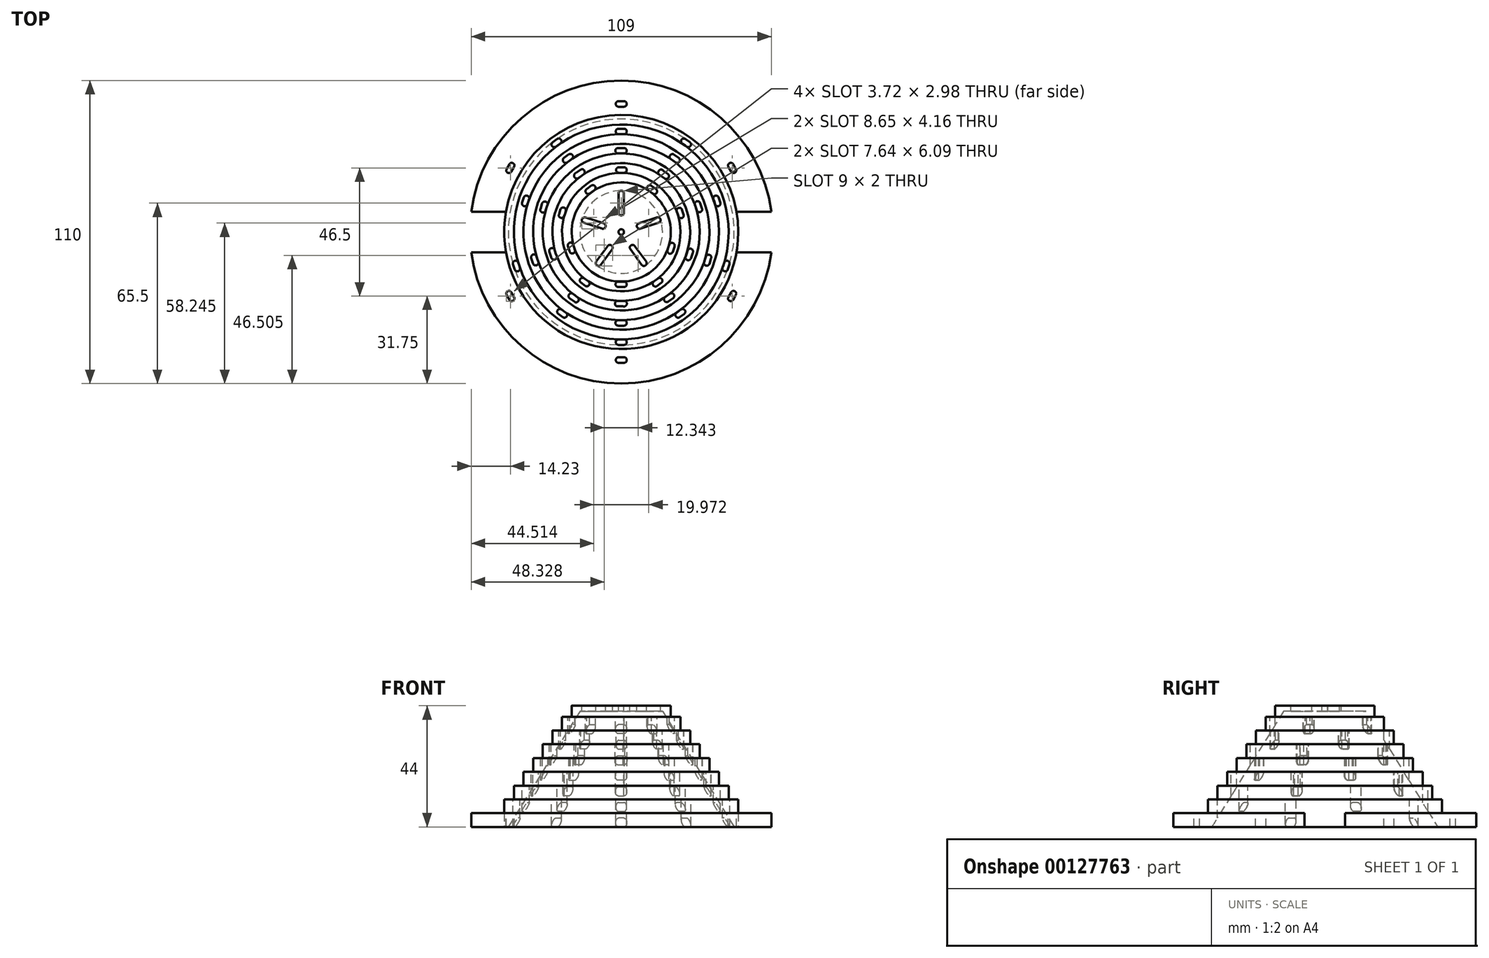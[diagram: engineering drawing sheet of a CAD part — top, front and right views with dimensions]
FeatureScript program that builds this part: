
annotation { "Feature Type Name" : "Feature", "Feature Type Description" : "" }
export const myFeature = defineFeature(function(context is Context, id is Id, definition is map)
    precondition{}
    {
        {
            var Q0;
            Q0=qCreatedBy(makeId("Top.planeOp"),FACE);
            var sketch = newSketch(context, id + "F0", { "sketchPlane" : qUnion([Q0])});
            skCircle(sketch, "E0", {"center": v(0, 0) * mm, "radius": 55 * mm});
            skSolve(sketch);
        }
        {
            var Q0;
            Q0 = qSketchRegion(id + "F0", true);
            extrude(context, id + "F1", {"entities" : qUnion([Q0]), "depth" : 5 * mm});
        }
        {
            var Q0;
            Q0=makeQuery(id+"F1.opExtrude","CAP_FACE",FACE,{"disambiguationData":[OSD([sQuery(id+"F0.wireOp",EDGE,"E0")])],"isStart":false});
            var sketch = newSketch(context, id + "F2", { "sketchPlane" : qUnion([Q0])});
            skCircle(sketch, "E1.0", {"center": v(0, 0) * mm, "radius": 42.5 * mm});
            skSolve(sketch);
        }
        {
            var Q0;
            Q0 = qSketchRegion(id + "F2", true);
            extrude(context, id + "F3", {"entities" : qUnion([Q0]), "operationType" : NewBodyOperationType.ADD, "depth" : 5 * mm});
        }
        {
            var Q0;
            Q0=makeQuery(id+"F3.opExtrude","CAP_FACE",FACE,{"disambiguationData":[OSD([sQuery(id+"F2.wireOp",EDGE,"E1.0")])],"isStart":false});
            var sketch = newSketch(context, id + "F4", { "sketchPlane" : qUnion([Q0])});
            skLineSegment(sketch, "E2", {"start": v(0, 0) * mm, "end": v(0, -39) * mm, "construction": true});
            skLineSegment(sketch, "E3", {"start": v(-1, -39) * mm, "end": v(1, -39) * mm});
            skLineSegment(sketch, "E4", {"start": v(-1, -39) * mm, "end": v(-1, -40) * mm, "construction": true});
            skArc(sketch, "E5", {"start": v(-1, -39) * mm, "mid": v(-2, -40) * mm, "end": v(-1, -41) * mm});
            skArc(sketch, "E6.MirrorC", {"start": v(1, -39) * mm, "mid": v(2, -40) * mm, "end": v(1, -41) * mm});
            skLineSegment(sketch, "E7", {"start": v(-1, -41) * mm, "end": v(1, -41) * mm});
            skLineSegment(sketch, "E8.1.0", {"start": v(36.78, -13) * mm, "end": v(37.4, -11.1) * mm});
            skArc(sketch, "E8.1.1", {"start": v(36.78, -13) * mm, "mid": v(37.42, -14.26) * mm, "end": v(38.68, -13.62) * mm});
            skLineSegment(sketch, "E8.1.2", {"start": v(38.68, -13.62) * mm, "end": v(39.3, -11.72) * mm});
            skArc(sketch, "E8.1.3", {"start": v(37.4, -11.1) * mm, "mid": v(38.66, -10.46) * mm, "end": v(39.3, -11.72) * mm});
            skLineSegment(sketch, "E8.2.0", {"start": v(23.73, 30.96) * mm, "end": v(22.11, 32.14) * mm});
            skArc(sketch, "E8.2.1", {"start": v(23.73, 30.96) * mm, "mid": v(25.13, 31.19) * mm, "end": v(24.9, 32.58) * mm});
            skLineSegment(sketch, "E8.2.2", {"start": v(24.9, 32.58) * mm, "end": v(23.3, 33.76) * mm});
            skArc(sketch, "E8.2.3", {"start": v(22.11, 32.14) * mm, "mid": v(21.9, 33.54) * mm, "end": v(23.3, 33.76) * mm});
            skLineSegment(sketch, "E8.3.0", {"start": v(-22.11, 32.14) * mm, "end": v(-23.73, 30.96) * mm});
            skArc(sketch, "E8.3.1", {"start": v(-22.11, 32.14) * mm, "mid": v(-21.9, 33.54) * mm, "end": v(-23.3, 33.76) * mm});
            skLineSegment(sketch, "E8.3.2", {"start": v(-23.3, 33.76) * mm, "end": v(-24.9, 32.58) * mm});
            skArc(sketch, "E8.3.3", {"start": v(-23.73, 30.96) * mm, "mid": v(-25.13, 31.19) * mm, "end": v(-24.9, 32.58) * mm});
            skLineSegment(sketch, "E8.4.0", {"start": v(-37.4, -11.1) * mm, "end": v(-36.78, -13) * mm});
            skArc(sketch, "E8.4.1", {"start": v(-37.4, -11.1) * mm, "mid": v(-38.66, -10.46) * mm, "end": v(-39.3, -11.72) * mm});
            skLineSegment(sketch, "E8.4.2", {"start": v(-39.3, -11.72) * mm, "end": v(-38.68, -13.62) * mm});
            skArc(sketch, "E8.4.3", {"start": v(-36.78, -13) * mm, "mid": v(-37.42, -14.26) * mm, "end": v(-38.68, -13.62) * mm});
            skPoint(sketch, "E8.center", {"position": v(0, 0) * mm});
            skSolve(sketch);
        }
        {
            var Q0;
            Q0 = qSketchRegion(id + "F4", true);
            extrude(context, id + "F5", {"entities" : qUnion([Q0]), "operationType" : NewBodyOperationType.REMOVE, "endBound" : BoundingType.THROUGH_ALL, "oppositeDirection" : true, "depth" : 25 * mm});
        }
        {
            var Q0;
            Q0=makeQuery(id+"F1.opExtrude","CAP_FACE",FACE,{"disambiguationData":[OSD([sQuery(id+"F0.wireOp",EDGE,"E0")])],"isStart":false});
            var sketch = newSketch(context, id + "F6", { "sketchPlane" : qUnion([Q0])});
            skLineSegment(sketch, "E9", {"start": v(0, 0) * mm, "end": v(0, 45.5) * mm, "construction": true});
            skLineSegment(sketch, "E10", {"start": v(-1, 45.5) * mm, "end": v(1, 45.5) * mm});
            skLineSegment(sketch, "E11", {"start": v(-1, 45.5) * mm, "end": v(-1, 46.5) * mm, "construction": true});
            skArc(sketch, "E12", {"start": v(-1, 47.5) * mm, "mid": v(-2, 46.5) * mm, "end": v(-1, 45.5) * mm});
            skArc(sketch, "E13.MirrorC", {"start": v(1, 47.5) * mm, "mid": v(2, 46.5) * mm, "end": v(1, 45.5) * mm});
            skLineSegment(sketch, "E14", {"start": v(-1, 47.5) * mm, "end": v(1, 47.5) * mm});
            skArc(sketch, "E15.1.0", {"start": v(-41.64, 22.88) * mm, "mid": v(-41.27, 21.52) * mm, "end": v(-39.9, 21.88) * mm});
            skLineSegment(sketch, "E15.1.1", {"start": v(-41.64, 22.88) * mm, "end": v(-40.64, 24.62) * mm});
            skArc(sketch, "E15.1.2", {"start": v(-40.64, 24.62) * mm, "mid": v(-39.27, 24.98) * mm, "end": v(-38.9, 23.62) * mm});
            skLineSegment(sketch, "E15.1.3", {"start": v(-39.9, 21.88) * mm, "end": v(-38.9, 23.62) * mm});
            skArc(sketch, "E15.2.0", {"start": v(-40.64, -24.62) * mm, "mid": v(-39.27, -24.98) * mm, "end": v(-38.9, -23.62) * mm});
            skLineSegment(sketch, "E15.2.1", {"start": v(-40.64, -24.62) * mm, "end": v(-41.64, -22.88) * mm});
            skArc(sketch, "E15.2.2", {"start": v(-41.64, -22.88) * mm, "mid": v(-41.27, -21.52) * mm, "end": v(-39.9, -21.88) * mm});
            skLineSegment(sketch, "E15.2.3", {"start": v(-38.9, -23.62) * mm, "end": v(-39.9, -21.88) * mm});
            skArc(sketch, "E15.3.0", {"start": v(1, -47.5) * mm, "mid": v(2, -46.5) * mm, "end": v(1, -45.5) * mm});
            skLineSegment(sketch, "E15.3.1", {"start": v(1, -47.5) * mm, "end": v(-1, -47.5) * mm});
            skArc(sketch, "E15.3.2", {"start": v(-1, -47.5) * mm, "mid": v(-2, -46.5) * mm, "end": v(-1, -45.5) * mm});
            skLineSegment(sketch, "E15.3.3", {"start": v(1, -45.5) * mm, "end": v(-1, -45.5) * mm});
            skArc(sketch, "E15.4.0", {"start": v(41.64, -22.88) * mm, "mid": v(41.27, -21.52) * mm, "end": v(39.9, -21.88) * mm});
            skLineSegment(sketch, "E15.4.1", {"start": v(41.64, -22.88) * mm, "end": v(40.64, -24.62) * mm});
            skArc(sketch, "E15.4.2", {"start": v(40.64, -24.62) * mm, "mid": v(39.27, -24.98) * mm, "end": v(38.9, -23.62) * mm});
            skLineSegment(sketch, "E15.4.3", {"start": v(39.9, -21.88) * mm, "end": v(38.9, -23.62) * mm});
            skArc(sketch, "E15.5.0", {"start": v(40.64, 24.62) * mm, "mid": v(39.27, 24.98) * mm, "end": v(38.9, 23.62) * mm});
            skLineSegment(sketch, "E15.5.1", {"start": v(40.64, 24.62) * mm, "end": v(41.64, 22.88) * mm});
            skArc(sketch, "E15.5.2", {"start": v(41.64, 22.88) * mm, "mid": v(41.27, 21.52) * mm, "end": v(39.9, 21.88) * mm});
            skLineSegment(sketch, "E15.5.3", {"start": v(38.9, 23.62) * mm, "end": v(39.9, 21.88) * mm});
            skPoint(sketch, "E15.center", {"position": v(0, 0) * mm});
            skSolve(sketch);
        }
        {
            var Q0;
            Q0 = qSketchRegion(id + "F6", true);
            extrude(context, id + "F7", {"entities" : qUnion([Q0]), "operationType" : NewBodyOperationType.REMOVE, "endBound" : BoundingType.THROUGH_ALL, "oppositeDirection" : true, "depth" : 25 * mm});
        }
        {
            var Q0;
            Q0=makeQuery(id+"F3.opExtrude","CAP_FACE",FACE,{"disambiguationData":[OSD([sQuery(id+"F2.wireOp",EDGE,"E1.0")])],"isStart":false});
            var sketch = newSketch(context, id + "F8", { "sketchPlane" : qUnion([Q0])});
            skCircle(sketch, "E16.0", {"center": v(0, 0) * mm, "radius": 39 * mm});
            skSolve(sketch);
        }
        {
            var Q0;
            Q0 = qSketchRegion(id + "F8", true);
            extrude(context, id + "F9", {"entities" : qUnion([Q0]), "operationType" : NewBodyOperationType.ADD, "depth" : 5 * mm});
        }
        {
            var Q0;
            Q0=makeQuery(id+"F9.opExtrude","CAP_FACE",FACE,{"disambiguationData":[OSD([sQuery(id+"F8.wireOp",EDGE,"E16.0")])],"isStart":false});
            var sketch = newSketch(context, id + "F10", { "sketchPlane" : qUnion([Q0])});
            skLineSegment(sketch, "E17", {"start": v(0, 0) * mm, "end": v(0, 35.5) * mm, "construction": true});
            skLineSegment(sketch, "E18.0", {"start": v(1, 37.5) * mm, "end": v(-1, 37.5) * mm});
            skArc(sketch, "E19.0", {"start": v(-1, 37.5) * mm, "mid": v(-2, 36.5) * mm, "end": v(-1, 35.5) * mm});
            skLineSegment(sketch, "E20.0", {"start": v(1, 35.5) * mm, "end": v(-1, 35.5) * mm});
            skArc(sketch, "E21.0", {"start": v(1, 37.5) * mm, "mid": v(2, 36.5) * mm, "end": v(1, 35.5) * mm});
            skLineSegment(sketch, "E22.1.0", {"start": v(-35.36, 12.54) * mm, "end": v(-35.97, 10.64) * mm});
            skArc(sketch, "E22.1.1", {"start": v(-35.97, 10.64) * mm, "mid": v(-35.33, 9.38) * mm, "end": v(-34.07, 10.02) * mm});
            skLineSegment(sketch, "E22.1.2", {"start": v(-33.45, 11.92) * mm, "end": v(-34.07, 10.02) * mm});
            skArc(sketch, "E22.1.3", {"start": v(-35.36, 12.54) * mm, "mid": v(-34.1, 13.18) * mm, "end": v(-33.45, 11.92) * mm});
            skLineSegment(sketch, "E22.2.0", {"start": v(-22.85, -29.75) * mm, "end": v(-21.23, -30.93) * mm});
            skArc(sketch, "E22.2.1", {"start": v(-21.23, -30.93) * mm, "mid": v(-19.84, -30.7) * mm, "end": v(-20.06, -29.3) * mm});
            skLineSegment(sketch, "E22.2.2", {"start": v(-21.68, -28.13) * mm, "end": v(-20.06, -29.3) * mm});
            skArc(sketch, "E22.2.3", {"start": v(-22.85, -29.75) * mm, "mid": v(-23.07, -28.35) * mm, "end": v(-21.68, -28.13) * mm});
            skLineSegment(sketch, "E22.3.0", {"start": v(21.23, -30.93) * mm, "end": v(22.85, -29.75) * mm});
            skArc(sketch, "E22.3.1", {"start": v(22.85, -29.75) * mm, "mid": v(23.07, -28.35) * mm, "end": v(21.68, -28.13) * mm});
            skLineSegment(sketch, "E22.3.2", {"start": v(20.06, -29.3) * mm, "end": v(21.68, -28.13) * mm});
            skArc(sketch, "E22.3.3", {"start": v(21.23, -30.93) * mm, "mid": v(19.84, -30.7) * mm, "end": v(20.06, -29.3) * mm});
            skLineSegment(sketch, "E22.4.0", {"start": v(35.97, 10.64) * mm, "end": v(35.36, 12.54) * mm});
            skArc(sketch, "E22.4.1", {"start": v(35.36, 12.54) * mm, "mid": v(34.1, 13.18) * mm, "end": v(33.45, 11.92) * mm});
            skLineSegment(sketch, "E22.4.2", {"start": v(34.07, 10.02) * mm, "end": v(33.45, 11.92) * mm});
            skArc(sketch, "E22.4.3", {"start": v(35.97, 10.64) * mm, "mid": v(35.33, 9.38) * mm, "end": v(34.07, 10.02) * mm});
            skPoint(sketch, "E22.center", {"position": v(0, 0) * mm});
            skSolve(sketch);
        }
        {
            var Q0;
            Q0 = qSketchRegion(id + "F10", true);
            extrude(context, id + "F11", {"entities" : qUnion([Q0]), "operationType" : NewBodyOperationType.REMOVE, "endBound" : BoundingType.THROUGH_ALL, "oppositeDirection" : true, "depth" : 25 * mm});
        }
        {
            var Q0;
            Q0=makeQuery(id+"F9.opExtrude","CAP_FACE",FACE,{"disambiguationData":[OSD([sQuery(id+"F8.wireOp",EDGE,"E16.0")])],"isStart":false});
            var sketch = newSketch(context, id + "F12", { "sketchPlane" : qUnion([Q0])});
            skCircle(sketch, "E23.0", {"center": v(0, 0) * mm, "radius": 35.5 * mm});
            skSolve(sketch);
        }
        {
            var Q0;
            {var subQ0=sQuery(id+"F12.wireOp",EDGE,"E23.0");var subQ5=makeQuery(id+"F12.imprint","INTERSECT",VERTEX,{"derivedFrom":[makeQuery(id+"F11.boolean.opBoolean","COPY",EDGE,{"derivedFrom":makeQuery(id+"F11.opExtrude","CAP_EDGE",EDGE,{"disambiguationData":[OSD([sQuery(id+"F10.wireOp",EDGE,"E20.0")])],"isStart":true})}),subQ0]});Q0=makeQuery(id+"F12.imprint","IMPRINT",FACE,{"disambiguationData":[TD([[makeQuery(id+"F12.imprint","IMPRINT",EDGE,{"disambiguationData":[TD([[subQ5,1.0]])],"derivedFrom":subQ0}),1.0]])]});}
            extrude(context, id + "F13", {"entities" : qUnion([Q0]), "operationType" : NewBodyOperationType.ADD, "depth" : 5 * mm});
        }
        {
            var Q0;
            Q0=makeQuery(id+"F13.opExtrude","CAP_FACE",FACE,{"disambiguationData":[OSD([sQuery(id+"F12.wireOp",EDGE,"E23.0")])],"isStart":false});
            var sketch = newSketch(context, id + "F14", { "sketchPlane" : qUnion([Q0])});
            skLineSegment(sketch, "E24", {"start": v(0, 0) * mm, "end": v(0, -32) * mm, "construction": true});
            skLineSegment(sketch, "E25.0", {"start": v(1.1, -32) * mm, "end": v(-1.1, -32) * mm});
            skArc(sketch, "E26.0", {"start": v(-1.1, -32) * mm, "mid": v(-2.1, -33) * mm, "end": v(-1.1, -34) * mm});
            skLineSegment(sketch, "E27.0", {"start": v(0.9, -34) * mm, "end": v(-1.1, -34) * mm});
            skArc(sketch, "E28.0", {"start": v(1.1, -32) * mm, "mid": v(2, -33.1) * mm, "end": v(0.9, -34) * mm});
            skLineSegment(sketch, "E29.1.0", {"start": v(30.77, -8.84) * mm, "end": v(30.1, -10.93) * mm});
            skArc(sketch, "E29.1.1", {"start": v(30.1, -10.93) * mm, "mid": v(30.74, -12.2) * mm, "end": v(32, -11.55) * mm});
            skLineSegment(sketch, "E29.1.2", {"start": v(32.61, -9.65) * mm, "end": v(32, -11.55) * mm});
            skArc(sketch, "E29.1.3", {"start": v(30.77, -8.84) * mm, "mid": v(32.1, -8.33) * mm, "end": v(32.61, -9.65) * mm});
            skLineSegment(sketch, "E29.2.0", {"start": v(17.92, 26.53) * mm, "end": v(19.7, 25.24) * mm});
            skArc(sketch, "E29.2.1", {"start": v(19.7, 25.24) * mm, "mid": v(21.1, 25.46) * mm, "end": v(20.87, 26.86) * mm});
            skLineSegment(sketch, "E29.2.2", {"start": v(19.26, 28.04) * mm, "end": v(20.87, 26.86) * mm});
            skArc(sketch, "E29.2.3", {"start": v(17.92, 26.53) * mm, "mid": v(17.84, 27.95) * mm, "end": v(19.26, 28.04) * mm});
            skLineSegment(sketch, "E29.3.0", {"start": v(-19.7, 25.24) * mm, "end": v(-17.92, 26.53) * mm});
            skArc(sketch, "E29.3.1", {"start": v(-17.92, 26.53) * mm, "mid": v(-17.7, 27.93) * mm, "end": v(-19.1, 28.15) * mm});
            skLineSegment(sketch, "E29.3.2", {"start": v(-20.71, 26.98) * mm, "end": v(-19.1, 28.15) * mm});
            skArc(sketch, "E29.3.3", {"start": v(-19.7, 25.24) * mm, "mid": v(-21.07, 25.6) * mm, "end": v(-20.71, 26.98) * mm});
            skLineSegment(sketch, "E29.4.0", {"start": v(-30.1, -10.93) * mm, "end": v(-30.77, -8.84) * mm});
            skArc(sketch, "E29.4.1", {"start": v(-30.77, -8.84) * mm, "mid": v(-32.03, -8.2) * mm, "end": v(-32.68, -9.46) * mm});
            skLineSegment(sketch, "E29.4.2", {"start": v(-32.06, -11.36) * mm, "end": v(-32.68, -9.46) * mm});
            skArc(sketch, "E29.4.3", {"start": v(-30.1, -10.93) * mm, "mid": v(-30.86, -12.13) * mm, "end": v(-32.06, -11.36) * mm});
            skPoint(sketch, "E29.center", {"position": v(0, 0) * mm});
            skSolve(sketch);
        }
        {
            var Q0;
            Q0 = qSketchRegion(id + "F14", true);
            extrude(context, id + "F15", {"entities" : qUnion([Q0]), "operationType" : NewBodyOperationType.REMOVE, "endBound" : BoundingType.THROUGH_ALL, "oppositeDirection" : true, "depth" : 25 * mm});
        }
        {
            var Q0;
            Q0=makeQuery(id+"F13.opExtrude","CAP_FACE",FACE,{"disambiguationData":[OSD([sQuery(id+"F12.wireOp",EDGE,"E23.0")])],"isStart":false});
            var sketch = newSketch(context, id + "F16", { "sketchPlane" : qUnion([Q0])});
            skCircle(sketch, "E30.0", {"center": v(0, 0) * mm, "radius": 32 * mm});
            skLineSegment(sketch, "E31", {"start": v(0, 0) * mm, "end": v(0, 28.5) * mm, "construction": true});
            skLineSegment(sketch, "E32.0", {"start": v(0.87, 30.5) * mm, "end": v(-1.13, 30.5) * mm});
            skArc(sketch, "E33.0", {"start": v(-1.13, 30.5) * mm, "mid": v(-2.13, 29.5) * mm, "end": v(-1.13, 28.5) * mm});
            skLineSegment(sketch, "E34.0", {"start": v(1.13, 28.5) * mm, "end": v(-1.13, 28.5) * mm});
            skArc(sketch, "E35.0", {"start": v(0.87, 30.5) * mm, "mid": v(2, 29.63) * mm, "end": v(1.13, 28.5) * mm});
            skArc(sketch, "E36.1.0", {"start": v(-29.36, 8.35) * mm, "mid": v(-28.71, 7.09) * mm, "end": v(-27.45, 7.73) * mm});
            skLineSegment(sketch, "E36.1.1", {"start": v(-28.74, 10.25) * mm, "end": v(-29.36, 8.35) * mm});
            skArc(sketch, "E36.1.2", {"start": v(-28.74, 10.25) * mm, "mid": v(-27.56, 11.06) * mm, "end": v(-26.76, 9.88) * mm});
            skLineSegment(sketch, "E36.1.3", {"start": v(-26.76, 9.88) * mm, "end": v(-27.45, 7.73) * mm});
            skArc(sketch, "E36.2.0", {"start": v(-17.01, -25.34) * mm, "mid": v(-15.62, -25.12) * mm, "end": v(-15.84, -23.72) * mm});
            skLineSegment(sketch, "E36.2.1", {"start": v(-18.63, -24.16) * mm, "end": v(-17.01, -25.34) * mm});
            skArc(sketch, "E36.2.2", {"start": v(-18.63, -24.16) * mm, "mid": v(-19.03, -22.8) * mm, "end": v(-17.67, -22.4) * mm});
            skLineSegment(sketch, "E36.2.3", {"start": v(-17.67, -22.4) * mm, "end": v(-15.84, -23.72) * mm});
            skArc(sketch, "E36.3.0", {"start": v(18.84, -24.01) * mm, "mid": v(19.06, -22.61) * mm, "end": v(17.67, -22.4) * mm});
            skLineSegment(sketch, "E36.3.1", {"start": v(17.22, -25.19) * mm, "end": v(18.84, -24.01) * mm});
            skArc(sketch, "E36.3.2", {"start": v(17.22, -25.19) * mm, "mid": v(15.8, -25.15) * mm, "end": v(15.84, -23.72) * mm});
            skLineSegment(sketch, "E36.3.3", {"start": v(15.84, -23.72) * mm, "end": v(17.67, -22.4) * mm});
            skArc(sketch, "E36.4.0", {"start": v(28.66, 10.5) * mm, "mid": v(27.4, 11.14) * mm, "end": v(26.76, 9.88) * mm});
            skLineSegment(sketch, "E36.4.1", {"start": v(29.28, 8.6) * mm, "end": v(28.66, 10.5) * mm});
            skArc(sketch, "E36.4.2", {"start": v(29.28, 8.6) * mm, "mid": v(28.8, 7.25) * mm, "end": v(27.45, 7.73) * mm});
            skLineSegment(sketch, "E36.4.3", {"start": v(27.45, 7.73) * mm, "end": v(26.76, 9.88) * mm});
            skSolve(sketch);
        }
        {
            var Q0;
            Q0 = qSketchRegion(id + "F16", true);
            extrude(context, id + "F17", {"entities" : qUnion([Q0]), "operationType" : NewBodyOperationType.ADD, "depth" : 5 * mm});
        }
        {
            var Q0;
            Q0=makeQuery(id+"F17.opExtrude","CAP_FACE",FACE,{"disambiguationData":[OSD([sQuery(id+"F16.wireOp",EDGE,"E30.0"),sQuery(id+"F16.wireOp",EDGE,"E32.0"),sQuery(id+"F16.wireOp",EDGE,"E33.0"),sQuery(id+"F16.wireOp",EDGE,"E34.0"),sQuery(id+"F16.wireOp",EDGE,"E35.0"),sQuery(id+"F16.wireOp",EDGE,"E36.1.0"),sQuery(id+"F16.wireOp",EDGE,"E36.1.1"),sQuery(id+"F16.wireOp",EDGE,"E36.1.2"),sQuery(id+"F16.wireOp",EDGE,"E36.1.3"),sQuery(id+"F16.wireOp",EDGE,"E36.2.0"),sQuery(id+"F16.wireOp",EDGE,"E36.2.1"),sQuery(id+"F16.wireOp",EDGE,"E36.2.2"),sQuery(id+"F16.wireOp",EDGE,"E36.2.3"),sQuery(id+"F16.wireOp",EDGE,"E36.3.0"),sQuery(id+"F16.wireOp",EDGE,"E36.3.1"),sQuery(id+"F16.wireOp",EDGE,"E36.3.2"),sQuery(id+"F16.wireOp",EDGE,"E36.3.3"),sQuery(id+"F16.wireOp",EDGE,"E36.4.0"),sQuery(id+"F16.wireOp",EDGE,"E36.4.1"),sQuery(id+"F16.wireOp",EDGE,"E36.4.2"),sQuery(id+"F16.wireOp",EDGE,"E36.4.3")])],"isStart":false});
            var sketch = newSketch(context, id + "F18", { "sketchPlane" : qUnion([Q0])});
            skCircle(sketch, "E37.0", {"center": v(0, 0) * mm, "radius": 28.5 * mm});
            skSolve(sketch);
        }
        {
            var Q0;
            {var subQ0=sQuery(id+"F18.wireOp",EDGE,"E37.0");var subQ4=makeQuery(id+"F18.imprint","INTERSECT",VERTEX,{"derivedFrom":[makeQuery(id+"F17.opExtrude","CAP_EDGE",EDGE,{"disambiguationData":[OSD([sQuery(id+"F16.wireOp",EDGE,"E34.0")])],"isStart":false}),subQ0]});Q0=makeQuery(id+"F18.imprint","IMPRINT",FACE,{"disambiguationData":[TD([[makeQuery(id+"F18.imprint","IMPRINT",EDGE,{"disambiguationData":[TD([[subQ4,1.0]])],"derivedFrom":subQ0}),1.0]])]});}
            extrude(context, id + "F19", {"entities" : qUnion([Q0]), "operationType" : NewBodyOperationType.ADD, "depth" : 5 * mm});
        }
        {
            var Q0;
            Q0=makeQuery(id+"F19.opExtrude","CAP_FACE",FACE,{"disambiguationData":[OSD([sQuery(id+"F18.wireOp",EDGE,"E37.0")])],"isStart":false});
            var sketch = newSketch(context, id + "F20", { "sketchPlane" : qUnion([Q0])});
            skLineSegment(sketch, "E38", {"start": v(0, 0) * mm, "end": v(0, -25) * mm, "construction": true});
            skLineSegment(sketch, "E39.0", {"start": v(1.3, -25) * mm, "end": v(-1.3, -25) * mm});
            skArc(sketch, "E40.0", {"start": v(-1.3, -25) * mm, "mid": v(-2.3, -26) * mm, "end": v(-1.3, -27) * mm});
            skLineSegment(sketch, "E41.0", {"start": v(0.7, -27) * mm, "end": v(-1.3, -27) * mm});
            skArc(sketch, "E42.0", {"start": v(1.3, -25) * mm, "mid": v(2, -26.3) * mm, "end": v(0.7, -27) * mm});
            skArc(sketch, "E43.1.0", {"start": v(23.38, -8.96) * mm, "mid": v(24.02, -10.22) * mm, "end": v(25.28, -9.57) * mm});
            skLineSegment(sketch, "E43.1.1", {"start": v(25.9, -7.67) * mm, "end": v(25.28, -9.57) * mm});
            skArc(sketch, "E43.1.2", {"start": v(24.18, -6.5) * mm, "mid": v(25.63, -6.22) * mm, "end": v(25.9, -7.67) * mm});
            skLineSegment(sketch, "E43.1.3", {"start": v(24.18, -6.5) * mm, "end": v(23.38, -8.96) * mm});
            skArc(sketch, "E43.2.0", {"start": v(15.74, 19.46) * mm, "mid": v(17.14, 19.69) * mm, "end": v(16.92, 21.08) * mm});
            skLineSegment(sketch, "E43.2.1", {"start": v(15.3, 22.26) * mm, "end": v(16.92, 21.08) * mm});
            skArc(sketch, "E43.2.2", {"start": v(13.65, 20.99) * mm, "mid": v(13.84, 22.45) * mm, "end": v(15.3, 22.26) * mm});
            skLineSegment(sketch, "E43.2.3", {"start": v(13.65, 20.99) * mm, "end": v(15.74, 19.46) * mm});
            skArc(sketch, "E43.3.0", {"start": v(-13.65, 20.99) * mm, "mid": v(-13.43, 22.38) * mm, "end": v(-14.82, 22.6) * mm});
            skLineSegment(sketch, "E43.3.1", {"start": v(-16.44, 21.43) * mm, "end": v(-14.82, 22.6) * mm});
            skArc(sketch, "E43.3.2", {"start": v(-15.74, 19.46) * mm, "mid": v(-17.07, 20.1) * mm, "end": v(-16.44, 21.43) * mm});
            skLineSegment(sketch, "E43.3.3", {"start": v(-15.74, 19.46) * mm, "end": v(-13.65, 20.99) * mm});
            skArc(sketch, "E43.4.0", {"start": v(-24.18, -6.5) * mm, "mid": v(-25.44, -5.85) * mm, "end": v(-26.08, -7.11) * mm});
            skLineSegment(sketch, "E43.4.1", {"start": v(-25.46, -9.01) * mm, "end": v(-26.08, -7.11) * mm});
            skArc(sketch, "E43.4.2", {"start": v(-23.38, -8.96) * mm, "mid": v(-24.39, -10.03) * mm, "end": v(-25.46, -9.01) * mm});
            skLineSegment(sketch, "E43.4.3", {"start": v(-23.38, -8.96) * mm, "end": v(-24.18, -6.5) * mm});
            skPoint(sketch, "E43.center", {"position": v(0, 0) * mm});
            skSolve(sketch);
        }
        {
            var Q0;
            Q0 = qSketchRegion(id + "F20", true);
            extrude(context, id + "F21", {"entities" : qUnion([Q0]), "operationType" : NewBodyOperationType.REMOVE, "endBound" : BoundingType.THROUGH_ALL, "oppositeDirection" : true, "depth" : 25 * mm});
        }
        {
            var Q0;
            Q0=makeQuery(id+"F17.boolean.opBoolean","SPLIT",FACE,{"disambiguationData":[TD([makeQuery(id+"F17.opExtrude","SWEPT_FACE",FACE,{"disambiguationData":[OSD([sQuery(id+"F16.wireOp",EDGE,"E36.3.0")])]})])],"derivedFrom":makeQuery(id+"F13.opExtrude","CAP_FACE",FACE,{"disambiguationData":[OSD([sQuery(id+"F12.wireOp",EDGE,"E23.0")])],"isStart":false})});
            var Q1;
            Q1=makeQuery(id+"F17.boolean.opBoolean","SPLIT",FACE,{"disambiguationData":[TD([makeQuery(id+"F17.opExtrude","SWEPT_FACE",FACE,{"disambiguationData":[OSD([sQuery(id+"F16.wireOp",EDGE,"E36.4.0")])]})])],"derivedFrom":makeQuery(id+"F13.opExtrude","CAP_FACE",FACE,{"disambiguationData":[OSD([sQuery(id+"F12.wireOp",EDGE,"E23.0")])],"isStart":false})});
            var Q2;
            Q2=makeQuery(id+"F17.boolean.opBoolean","SPLIT",FACE,{"disambiguationData":[TD([makeQuery(id+"F17.opExtrude","SWEPT_FACE",FACE,{"disambiguationData":[OSD([sQuery(id+"F16.wireOp",EDGE,"E32.0")])]})])],"derivedFrom":makeQuery(id+"F13.opExtrude","CAP_FACE",FACE,{"disambiguationData":[OSD([sQuery(id+"F12.wireOp",EDGE,"E23.0")])],"isStart":false})});
            var Q3;
            Q3=makeQuery(id+"F17.boolean.opBoolean","SPLIT",FACE,{"disambiguationData":[TD([makeQuery(id+"F17.opExtrude","SWEPT_FACE",FACE,{"disambiguationData":[OSD([sQuery(id+"F16.wireOp",EDGE,"E36.1.0")])]})])],"derivedFrom":makeQuery(id+"F13.opExtrude","CAP_FACE",FACE,{"disambiguationData":[OSD([sQuery(id+"F12.wireOp",EDGE,"E23.0")])],"isStart":false})});
            var Q4;
            Q4=makeQuery(id+"F17.boolean.opBoolean","SPLIT",FACE,{"disambiguationData":[TD([makeQuery(id+"F17.opExtrude","SWEPT_FACE",FACE,{"disambiguationData":[OSD([sQuery(id+"F16.wireOp",EDGE,"E36.2.0")])]})])],"derivedFrom":makeQuery(id+"F13.opExtrude","CAP_FACE",FACE,{"disambiguationData":[OSD([sQuery(id+"F12.wireOp",EDGE,"E23.0")])],"isStart":false})});
            extrude(context, id + "F22", {"entities" : qUnion([Q0, Q1, Q2, Q3, Q4]), "operationType" : NewBodyOperationType.REMOVE, "endBound" : BoundingType.THROUGH_ALL, "oppositeDirection" : true, "depth" : 25 * mm});
        }
        {
            var Q0;
            Q0=makeQuery(id+"F19.opExtrude","CAP_FACE",FACE,{"disambiguationData":[OSD([sQuery(id+"F18.wireOp",EDGE,"E37.0")])],"isStart":false});
            var sketch = newSketch(context, id + "F23", { "sketchPlane" : qUnion([Q0])});
            skCircle(sketch, "E44.0", {"center": v(0, 0) * mm, "radius": 25 * mm});
            skSolve(sketch);
        }
        {
            var Q0;
            {var subQ0=sQuery(id+"F23.wireOp",EDGE,"E44.0");var subQ4=makeQuery(id+"F23.imprint","INTERSECT",VERTEX,{"derivedFrom":[makeQuery(id+"F21.boolean.opBoolean","COPY",EDGE,{"derivedFrom":makeQuery(id+"F21.opExtrude","CAP_EDGE",EDGE,{"disambiguationData":[OSD([sQuery(id+"F20.wireOp",EDGE,"E43.3.3")])],"isStart":true})}),subQ0]});Q0=makeQuery(id+"F23.imprint","IMPRINT",FACE,{"disambiguationData":[TD([[makeQuery(id+"F23.imprint","IMPRINT",EDGE,{"disambiguationData":[TD([[subQ4,1.0]])],"derivedFrom":subQ0}),1.0]])]});}
            extrude(context, id + "F24", {"entities" : qUnion([Q0]), "operationType" : NewBodyOperationType.ADD, "depth" : 5 * mm});
        }
        {
            var Q0;
            Q0=makeQuery(id+"F24.opExtrude","CAP_FACE",FACE,{"disambiguationData":[OSD([sQuery(id+"F23.wireOp",EDGE,"E44.0")])],"isStart":false});
            var sketch = newSketch(context, id + "F25", { "sketchPlane" : qUnion([Q0])});
            skLineSegment(sketch, "E45", {"start": v(0, 0) * mm, "end": v(0, 21.5) * mm, "construction": true});
            skLineSegment(sketch, "E46.0", {"start": v(1.11, 23.5) * mm, "end": v(-0.89, 23.5) * mm});
            skArc(sketch, "E47.0", {"start": v(-0.89, 23.5) * mm, "mid": v(-1.89, 22.5) * mm, "end": v(-0.89, 21.5) * mm});
            skLineSegment(sketch, "E48.0", {"start": v(0.89, 21.5) * mm, "end": v(-0.89, 21.5) * mm});
            skArc(sketch, "E49.0", {"start": v(1.11, 23.5) * mm, "mid": v(2, 22.39) * mm, "end": v(0.89, 21.5) * mm});
            skArc(sketch, "E50.1.0", {"start": v(-22.62, 6.42) * mm, "mid": v(-21.98, 5.16) * mm, "end": v(-20.72, 5.8) * mm});
            skLineSegment(sketch, "E50.1.1", {"start": v(-22, 8.32) * mm, "end": v(-22.62, 6.42) * mm});
            skArc(sketch, "E50.1.2", {"start": v(-22, 8.32) * mm, "mid": v(-20.68, 8.82) * mm, "end": v(-20.17, 7.49) * mm});
            skLineSegment(sketch, "E50.1.3", {"start": v(-20.17, 7.49) * mm, "end": v(-20.72, 5.8) * mm});
            skArc(sketch, "E50.2.0", {"start": v(-13.1, -19.53) * mm, "mid": v(-11.7, -19.31) * mm, "end": v(-11.92, -17.92) * mm});
            skLineSegment(sketch, "E50.2.1", {"start": v(-14.71, -18.36) * mm, "end": v(-13.1, -19.53) * mm});
            skArc(sketch, "E50.2.2", {"start": v(-14.71, -18.36) * mm, "mid": v(-14.78, -16.94) * mm, "end": v(-13.36, -16.87) * mm});
            skLineSegment(sketch, "E50.2.3", {"start": v(-13.36, -16.87) * mm, "end": v(-11.92, -17.92) * mm});
            skArc(sketch, "E50.3.0", {"start": v(14.53, -18.49) * mm, "mid": v(14.75, -17.1) * mm, "end": v(13.36, -16.87) * mm});
            skLineSegment(sketch, "E50.3.1", {"start": v(12.91, -19.66) * mm, "end": v(14.53, -18.49) * mm});
            skArc(sketch, "E50.3.2", {"start": v(12.91, -19.66) * mm, "mid": v(11.54, -19.29) * mm, "end": v(11.92, -17.92) * mm});
            skLineSegment(sketch, "E50.3.3", {"start": v(11.92, -17.92) * mm, "end": v(13.36, -16.87) * mm});
            skArc(sketch, "E50.4.0", {"start": v(22.07, 8.1) * mm, "mid": v(20.81, 8.75) * mm, "end": v(20.17, 7.49) * mm});
            skLineSegment(sketch, "E50.4.1", {"start": v(22.7, 6.2) * mm, "end": v(22.07, 8.1) * mm});
            skArc(sketch, "E50.4.2", {"start": v(22.7, 6.2) * mm, "mid": v(21.91, 5.02) * mm, "end": v(20.72, 5.8) * mm});
            skLineSegment(sketch, "E50.4.3", {"start": v(20.72, 5.8) * mm, "end": v(20.17, 7.49) * mm});
            skPoint(sketch, "E50.center", {"position": v(0, 0) * mm});
            skSolve(sketch);
        }
        {
            var Q0;
            Q0 = qSketchRegion(id + "F25", true);
            extrude(context, id + "F26", {"entities" : qUnion([Q0]), "operationType" : NewBodyOperationType.REMOVE, "endBound" : BoundingType.THROUGH_ALL, "oppositeDirection" : true, "depth" : 25 * mm});
        }
        {
            var Q0;
            Q0=makeQuery(id+"F24.opExtrude","CAP_FACE",FACE,{"disambiguationData":[OSD([sQuery(id+"F23.wireOp",EDGE,"E44.0")])],"isStart":false});
            var sketch = newSketch(context, id + "F27", { "sketchPlane" : qUnion([Q0])});
            skCircle(sketch, "E51.0", {"center": v(0, 0) * mm, "radius": 21.5 * mm});
            skSolve(sketch);
        }
        {
            var Q0;
            {var subQ0=sQuery(id+"F27.wireOp",EDGE,"E51.0");var subQ4=makeQuery(id+"F27.imprint","INTERSECT",VERTEX,{"derivedFrom":[makeQuery(id+"F26.boolean.opBoolean","COPY",EDGE,{"derivedFrom":makeQuery(id+"F26.opExtrude","CAP_EDGE",EDGE,{"disambiguationData":[OSD([sQuery(id+"F25.wireOp",EDGE,"E48.0")])],"isStart":true})}),subQ0]});Q0=makeQuery(id+"F27.imprint","IMPRINT",FACE,{"disambiguationData":[TD([[makeQuery(id+"F27.imprint","IMPRINT",EDGE,{"disambiguationData":[TD([[subQ4,1.0]])],"derivedFrom":subQ0}),1.0]])]});}
            extrude(context, id + "F28", {"entities" : qUnion([Q0]), "operationType" : NewBodyOperationType.ADD, "depth" : 5 * mm});
        }
        {
            var Q0;
            Q0=makeQuery(id+"F28.opExtrude","CAP_FACE",FACE,{"disambiguationData":[OSD([sQuery(id+"F27.wireOp",EDGE,"E51.0")])],"isStart":false});
            var sketch = newSketch(context, id + "F29", { "sketchPlane" : qUnion([Q0])});
            skLineSegment(sketch, "E52", {"start": v(0, 0) * mm, "end": v(0, -18) * mm, "construction": true});
            skLineSegment(sketch, "E53.0", {"start": v(-1, 45.5) * mm, "end": v(1, 45.5) * mm});
            skArc(sketch, "E53.1", {"start": v(-1, 47.5) * mm, "mid": v(-2, 46.5) * mm, "end": v(-1, 45.5) * mm});
            skLineSegment(sketch, "E53.2", {"start": v(-1, 47.5) * mm, "end": v(1, 47.5) * mm});
            skArc(sketch, "E53.3", {"start": v(1, 47.5) * mm, "mid": v(2, 46.5) * mm, "end": v(1, 45.5) * mm});
            skLineSegment(sketch, "E54.0", {"start": v(-1.07, -20) * mm, "end": v(0.93, -20) * mm});
            skArc(sketch, "E54.1", {"start": v(-1.07, -18) * mm, "mid": v(-2.07, -19) * mm, "end": v(-1.07, -20) * mm});
            skLineSegment(sketch, "E54.2", {"start": v(-1.07, -18) * mm, "end": v(1.07, -18) * mm});
            skArc(sketch, "E54.3", {"start": v(1.07, -18) * mm, "mid": v(2, -19.07) * mm, "end": v(0.93, -20) * mm});
            skLineSegment(sketch, "E55.1.0", {"start": v(16.79, -6.58) * mm, "end": v(17.45, -4.55) * mm});
            skArc(sketch, "E55.1.1", {"start": v(16.79, -6.58) * mm, "mid": v(17.43, -7.84) * mm, "end": v(18.7, -7.2) * mm});
            skLineSegment(sketch, "E55.1.2", {"start": v(18.7, -7.2) * mm, "end": v(19.3, -5.3) * mm});
            skArc(sketch, "E55.1.3", {"start": v(17.45, -4.55) * mm, "mid": v(18.75, -4) * mm, "end": v(19.3, -5.3) * mm});
            skLineSegment(sketch, "E55.2.0", {"start": v(11.45, 13.93) * mm, "end": v(9.71, 15.2) * mm});
            skArc(sketch, "E55.2.1", {"start": v(11.45, 13.93) * mm, "mid": v(12.84, 14.15) * mm, "end": v(12.62, 15.55) * mm});
            skLineSegment(sketch, "E55.2.2", {"start": v(12.62, 15.55) * mm, "end": v(11, 16.73) * mm});
            skArc(sketch, "E55.2.3", {"start": v(9.71, 15.2) * mm, "mid": v(9.6, 16.6) * mm, "end": v(11, 16.73) * mm});
            skLineSegment(sketch, "E55.3.0", {"start": v(-9.71, 15.2) * mm, "end": v(-11.45, 13.93) * mm});
            skArc(sketch, "E55.3.1", {"start": v(-9.71, 15.2) * mm, "mid": v(-9.5, 16.59) * mm, "end": v(-10.9, 16.8) * mm});
            skLineSegment(sketch, "E55.3.2", {"start": v(-10.9, 16.8) * mm, "end": v(-12.5, 15.63) * mm});
            skArc(sketch, "E55.3.3", {"start": v(-11.45, 13.93) * mm, "mid": v(-12.83, 14.25) * mm, "end": v(-12.5, 15.63) * mm});
            skLineSegment(sketch, "E55.4.0", {"start": v(-17.45, -4.55) * mm, "end": v(-16.79, -6.58) * mm});
            skArc(sketch, "E55.4.1", {"start": v(-17.45, -4.55) * mm, "mid": v(-18.7, -3.9) * mm, "end": v(-19.35, -5.16) * mm});
            skLineSegment(sketch, "E55.4.2", {"start": v(-19.35, -5.16) * mm, "end": v(-18.73, -7.07) * mm});
            skArc(sketch, "E55.4.3", {"start": v(-16.79, -6.58) * mm, "mid": v(-17.52, -7.8) * mm, "end": v(-18.73, -7.07) * mm});
            skPoint(sketch, "E55.center", {"position": v(0, 0) * mm});
            skSolve(sketch);
        }
        {
            var Q0;
            Q0 = qSketchRegion(id + "F29", true);
            extrude(context, id + "F30", {"entities" : qUnion([Q0]), "operationType" : NewBodyOperationType.REMOVE, "endBound" : BoundingType.THROUGH_ALL, "oppositeDirection" : true, "depth" : 25 * mm});
        }
        {
            var Q0;
            Q0=makeQuery(id+"F28.opExtrude","CAP_FACE",FACE,{"disambiguationData":[OSD([sQuery(id+"F27.wireOp",EDGE,"E51.0")])],"isStart":false});
            var sketch = newSketch(context, id + "F31", { "sketchPlane" : qUnion([Q0])});
            skCircle(sketch, "E56.0", {"center": v(0, 0) * mm, "radius": 18 * mm});
            skSolve(sketch);
        }
        {
            var Q0;
            {var subQ0=sQuery(id+"F31.wireOp",EDGE,"E56.0");var subQ4=makeQuery(id+"F31.imprint","INTERSECT",VERTEX,{"derivedFrom":[makeQuery(id+"F30.boolean.opBoolean","COPY",EDGE,{"derivedFrom":makeQuery(id+"F30.opExtrude","CAP_EDGE",EDGE,{"disambiguationData":[OSD([sQuery(id+"F29.wireOp",EDGE,"E55.3.0")])],"isStart":true})}),subQ0]});Q0=makeQuery(id+"F31.imprint","IMPRINT",FACE,{"disambiguationData":[TD([[makeQuery(id+"F31.imprint","IMPRINT",EDGE,{"disambiguationData":[TD([[subQ4,1.0]])],"derivedFrom":subQ0}),1.0]])]});}
            extrude(context, id + "F32", {"entities" : qUnion([Q0]), "operationType" : NewBodyOperationType.ADD, "depth" : 4 * mm});
        }
        {
            var Q0;
            Q0=makeQuery(id+"F32.opExtrude","CAP_FACE",FACE,{"disambiguationData":[OSD([sQuery(id+"F31.wireOp",EDGE,"E56.0")])],"isStart":false});
            var sketch = newSketch(context, id + "F33", { "sketchPlane" : qUnion([Q0])});
            skCircle(sketch, "E57", {"center": v(0, 0) * mm, "radius": 1 * mm});
            skLineSegment(sketch, "E58", {"start": v(0, 0) * mm, "end": v(0, 7) * mm, "construction": true});
            skArc(sketch, "E59", {"start": v(-1, 7) * mm, "mid": v(0, 6) * mm, "end": v(1, 7) * mm});
            skLineSegment(sketch, "E60", {"start": v(1, 7) * mm, "end": v(1, 14) * mm});
            skLineSegment(sketch, "E61.MirrorCS", {"start": v(-1, 7) * mm, "end": v(-1, 14) * mm});
            skArc(sketch, "E62", {"start": v(1, 14) * mm, "mid": v(0, 15) * mm, "end": v(-1, 14) * mm});
            skArc(sketch, "E63.1.0", {"start": v(-13, 5.28) * mm, "mid": v(-14.27, 4.64) * mm, "end": v(-13.62, 3.38) * mm});
            skLineSegment(sketch, "E63.1.1", {"start": v(-6.35, 3.11) * mm, "end": v(-13, 5.28) * mm});
            skArc(sketch, "E63.1.2", {"start": v(-6.97, 1.21) * mm, "mid": v(-5.7, 1.85) * mm, "end": v(-6.35, 3.11) * mm});
            skLineSegment(sketch, "E63.1.3", {"start": v(-6.97, 1.21) * mm, "end": v(-13.62, 3.38) * mm});
            skArc(sketch, "E63.2.0", {"start": v(-9.04, -10.74) * mm, "mid": v(-8.82, -12.14) * mm, "end": v(-7.42, -11.91) * mm});
            skLineSegment(sketch, "E63.2.1", {"start": v(-4.92, -5.08) * mm, "end": v(-9.04, -10.74) * mm});
            skArc(sketch, "E63.2.2", {"start": v(-3.3, -6.25) * mm, "mid": v(-3.53, -4.85) * mm, "end": v(-4.92, -5.08) * mm});
            skLineSegment(sketch, "E63.2.3", {"start": v(-3.3, -6.25) * mm, "end": v(-7.42, -11.91) * mm});
            skArc(sketch, "E63.3.0", {"start": v(7.42, -11.91) * mm, "mid": v(8.82, -12.14) * mm, "end": v(9.04, -10.74) * mm});
            skLineSegment(sketch, "E63.3.1", {"start": v(3.3, -6.25) * mm, "end": v(7.42, -11.91) * mm});
            skArc(sketch, "E63.3.2", {"start": v(4.92, -5.08) * mm, "mid": v(3.53, -4.85) * mm, "end": v(3.3, -6.25) * mm});
            skLineSegment(sketch, "E63.3.3", {"start": v(4.92, -5.08) * mm, "end": v(9.04, -10.74) * mm});
            skArc(sketch, "E63.4.0", {"start": v(13.62, 3.38) * mm, "mid": v(14.27, 4.64) * mm, "end": v(13, 5.28) * mm});
            skLineSegment(sketch, "E63.4.1", {"start": v(6.97, 1.21) * mm, "end": v(13.62, 3.38) * mm});
            skArc(sketch, "E63.4.2", {"start": v(6.35, 3.11) * mm, "mid": v(5.7, 1.85) * mm, "end": v(6.97, 1.21) * mm});
            skLineSegment(sketch, "E63.4.3", {"start": v(6.35, 3.11) * mm, "end": v(13, 5.28) * mm});
            skSolve(sketch);
        }
        {
            var Q0;
            Q0 = qSketchRegion(id + "F33", true);
            extrude(context, id + "F34", {"entities" : qUnion([Q0]), "operationType" : NewBodyOperationType.REMOVE, "endBound" : BoundingType.THROUGH_ALL, "oppositeDirection" : true, "depth" : 25 * mm});
        }
        {
            var Q0;
            Q0=makeQuery(id+"F32.opExtrude","CAP_FACE",FACE,{"disambiguationData":[OSD([sQuery(id+"F31.wireOp",EDGE,"E56.0")])],"isStart":false});
            cPlane(context, id + "F35", {"entities" : qUnion([Q0]), "cplaneType" : CPlaneType.OFFSET, "offset" : 2 * mm, "oppositeDirection" : true, "width" : 150 * mm, "height" : 150 * mm});
        }
        {
            var Q0;
            Q0=makeQuery(id+"F1.opExtrude","CAP_FACE",FACE,{"disambiguationData":[OSD([sQuery(id+"F0.wireOp",EDGE,"E0")])],"isStart":true});
            var sketch = newSketch(context, id + "F36", { "sketchPlane" : qUnion([Q0])});
            skCircle(sketch, "E64", {"center": v(0, 0) * mm, "radius": 41 * mm});
            skSolve(sketch);
        }
        {
            var Q0;
            Q0=qCreatedBy(id+"F35.planeOp",FACE);
            var sketch = newSketch(context, id + "F37", { "sketchPlane" : qUnion([Q0])});
            skCircle(sketch, "E65.0", {"center": v(0, 0) * mm, "radius": 18 * mm});
            skSolve(sketch);
        }
        {
            var Q0;
            Q0=qCreatedBy(makeId("Right.planeOp"),FACE);
            var sketch = newSketch(context, id + "F38", { "sketchPlane" : qUnion([Q0])});
            skLineSegment(sketch, "E66.0", {"start": v(-18, 42) * mm, "end": v(18, 42) * mm});
            skLineSegment(sketch, "E67.0", {"start": v(14, 44) * mm, "end": v(15, 44) * mm});
            skLineSegment(sketch, "E68.0", {"start": v(41, 0) * mm, "end": v(-41, 0) * mm});
            skLineSegment(sketch, "E69", {"start": v(15, 44) * mm, "end": v(15, 42) * mm, "construction": true});
            skLineSegment(sketch, "E70", {"start": v(41, 0) * mm, "end": v(0, 0) * mm});
            skLineSegment(sketch, "E71", {"start": v(0, 0) * mm, "end": v(0, 42) * mm});
            skLineSegment(sketch, "E72", {"start": v(0, 42) * mm, "end": v(15, 42) * mm});
            skLineSegment(sketch, "E73", {"start": v(15, 42) * mm, "end": v(41, 0) * mm});
            skSolve(sketch);
        }
        {
            var Q0;
            Q0 = qSketchRegion(id + "F38", true);
            var Q1;
            Q1=sQuery(id+"F38.wireOp",EDGE,"E71");
            revolve(context, id + "F39", {"operationType" : NewBodyOperationType.REMOVE, "entities" : qUnion([Q0]), "axis" : qUnion([Q1]), "revolveType" : RevolveType.FULL, "oppositeDirection" : true});
        }
        {
            var Q0;
            Q0=makeQuery(id+"F1.opExtrude","CAP_FACE",FACE,{"disambiguationData":[OSD([sQuery(id+"F0.wireOp",EDGE,"E0")])],"isStart":false});
            var sketch = newSketch(context, id + "F40", { "sketchPlane" : qUnion([Q0])});
            skLineSegment(sketch, "E74", {"start": v(-42.5, 0) * mm, "end": v(-55, 0) * mm, "construction": true});
            skLineSegment(sketch, "E75", {"start": v(0, 0) * mm, "end": v(0, -5.67) * mm, "construction": true});
            skLineSegment(sketch, "E76", {"start": v(-41.85, 7.4) * mm, "end": v(-54.5, 7.4) * mm});
            skLineSegment(sketch, "E77.MirrorCS", {"start": v(-41.85, -7.4) * mm, "end": v(-54.5, -7.4) * mm});
            skLineSegment(sketch, "E78.MirrorCS", {"start": v(41.85, 7.4) * mm, "end": v(54.5, 7.4) * mm});
            skLineSegment(sketch, "E79.MirrorCS", {"start": v(41.85, -7.4) * mm, "end": v(54.5, -7.4) * mm});
            skLineSegment(sketch, "E80", {"start": v(-41.85, 7.4) * mm, "end": v(-41.85, -7.4) * mm});
            skLineSegment(sketch, "E81", {"start": v(41.85, 7.4) * mm, "end": v(41.85, -7.4) * mm});
            skSolve(sketch);
        }
        {
            var Q0;
            {var subQ0=sQuery(id+"F40.wireOp",EDGE,"E76");Q0=makeQuery(id+"F40.imprint","IMPRINT",FACE,{"disambiguationData":[TD([[makeQuery(id+"F40.imprint","IMPRINT",EDGE,{"derivedFrom":subQ0}),1.0]])]});}
            var Q1;
            {var subQ0=sQuery(id+"F40.wireOp",EDGE,"E78.MirrorCS");Q1=makeQuery(id+"F40.imprint","IMPRINT",FACE,{"disambiguationData":[TD([[makeQuery(id+"F40.imprint","IMPRINT",EDGE,{"derivedFrom":subQ0}),-1.0]])]});}
            extrude(context, id + "F41", {"entities" : qUnion([Q0, Q1]), "operationType" : NewBodyOperationType.REMOVE, "endBound" : BoundingType.THROUGH_ALL, "oppositeDirection" : true, "depth" : 25 * mm});
        }
    });
